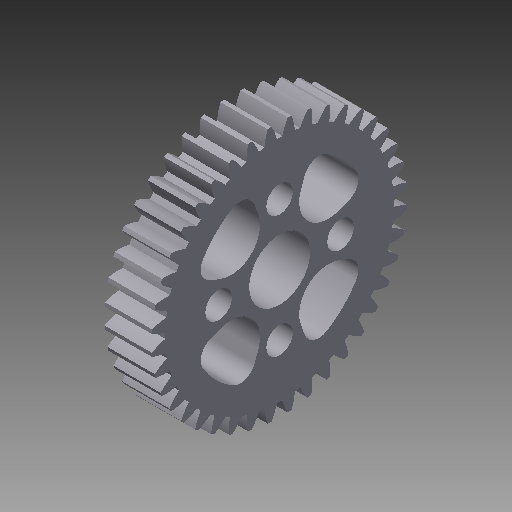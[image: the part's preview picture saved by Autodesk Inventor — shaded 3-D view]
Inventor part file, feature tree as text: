
AUTODESK INVENTOR PART (.ipt)
format: ipt  version: 2017 (Build 210142000, 142)  size: 391,168 bytes
history: native  units: in
note: dims shown in document units (in); Inventor stores cm internally (conversion verified against a paired STEP export)
features: imported_body x1, extrude x1, fillet x1, pattern_circular x1, sketch x1
ambient origin geometry x8: Origin, YZ Plane, XZ Plane, XY Plane, X Axis, Y Axis, Z Axis, Center Point
bodies: Solid1 (feature_tree)
feature tree (5):
  imported_body  "Base1"
  extrude  "Extrusion1"  Depth=0.1374in
  fillet  "Fillet1"  Radius=0.1374in
  pattern_circular  "Circular Pattern1"  [2 undecoded]
  sketch  "Sketch1"  dims[d0=0.125in d1=0.1374in d2=0.1374in d3=0.15in d4=0.3937in d5=0.0in d6=0.0787in d7=1.5748in d8=360.0deg]
note: 2 required parameter values undecoded (feature->parameter linkage not recoverable at this tier; creation-order binding heuristic only, values carry confidence <= 0.55)
